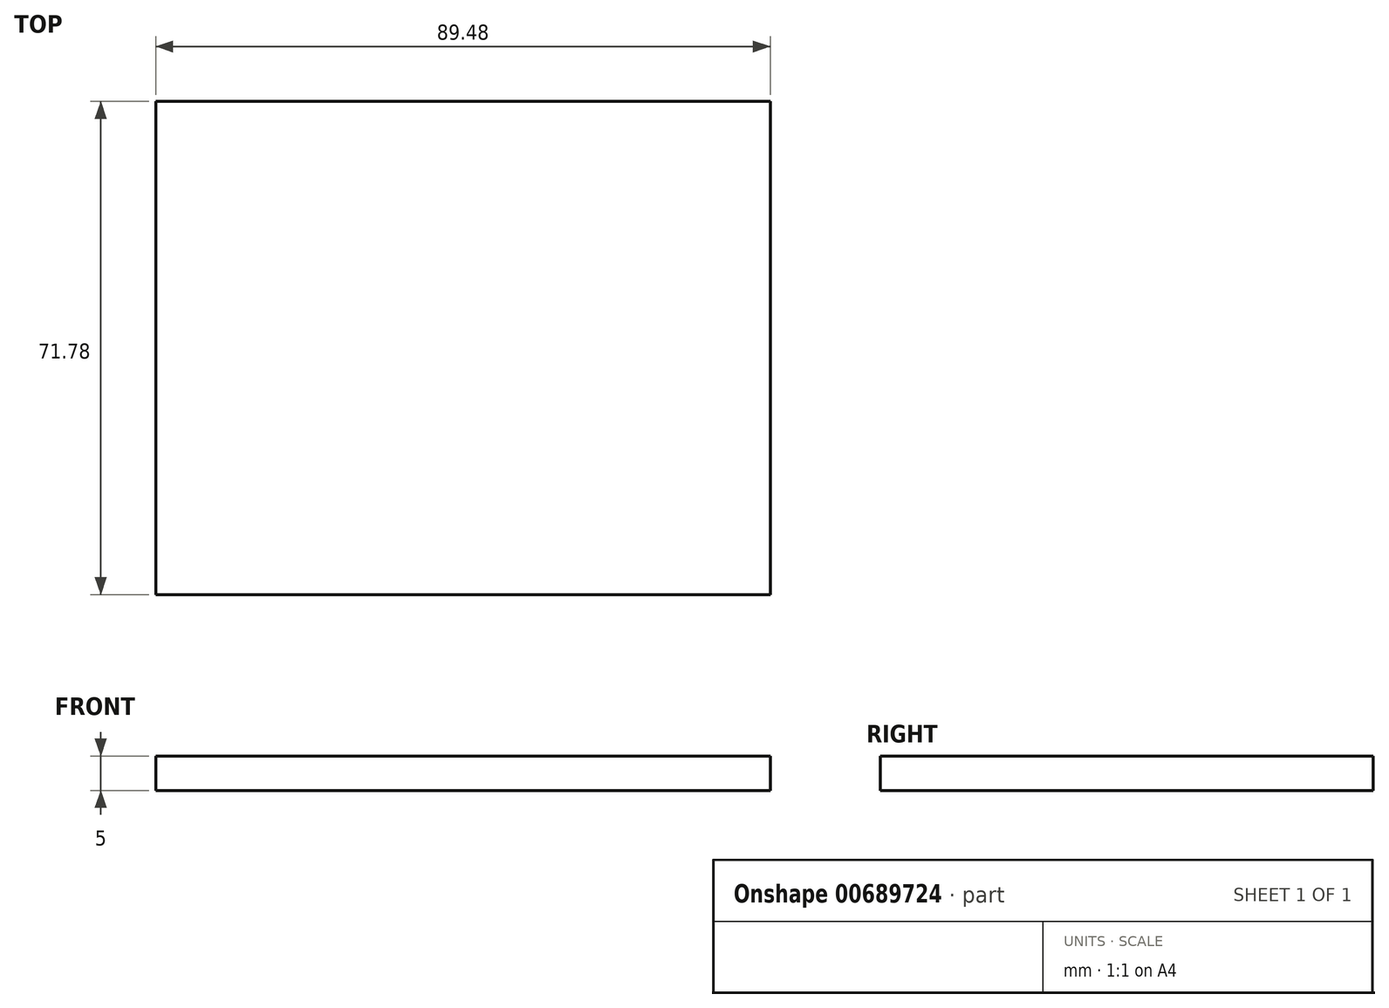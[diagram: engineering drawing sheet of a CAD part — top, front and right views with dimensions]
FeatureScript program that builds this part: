
annotation { "Feature Type Name" : "Feature", "Feature Type Description" : "" }
export const myFeature = defineFeature(function(context is Context, id is Id, definition is map)
    precondition{}
    {
        {
            var Q0;
            Q0=qCreatedBy(makeId("Top.planeOp"),FACE);
            var sketch = newSketch(context, id + "F0", { "sketchPlane" : qUnion([Q0])});
            skLineSegment(sketch, "E0.bottom", {"start": v(44.74, -35.9) * mm, "end": v(-44.74, -35.9) * mm});
            skLineSegment(sketch, "E0.top", {"start": v(44.74, 35.9) * mm, "end": v(-44.74, 35.9) * mm});
            skLineSegment(sketch, "E0.left", {"start": v(44.74, -35.9) * mm, "end": v(44.74, 35.9) * mm});
            skLineSegment(sketch, "E0.right", {"start": v(-44.74, -35.9) * mm, "end": v(-44.74, 35.9) * mm});
            skPoint(sketch, "E0.middle", {"position": v(0, 0) * mm});
            skSolve(sketch);
        }
        {
            var Q0;
            Q0=makeQuery(id+"F0.imprint","IMPRINT",FACE,{"disambiguationData":[TD([[makeQuery(id+"F0.imprint","IMPRINT",EDGE,{"derivedFrom":sQuery(id+"F0.wireOp",EDGE,"E0.bottom")}),-1.0]])]});
            extrude(context, id + "F1", {"entities" : qUnion([Q0]), "depth" : 5 * mm, "offsetDistance" : 25 * mm});
        }
    });
